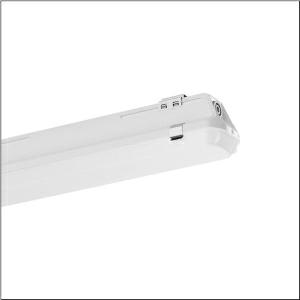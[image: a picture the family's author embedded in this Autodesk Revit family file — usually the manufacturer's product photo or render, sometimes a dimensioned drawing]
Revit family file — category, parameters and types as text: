
# Revit family: monsun_11_51fp12mp480h
name_source: partatom
category: Lighting Fixtures
units: mm (PartAtom-declared; Revit-internal decimal feet)

## family parameters
Cut with Voids When Loaded = No
Host = Face
Light Source = No
Part Type = Normal
Room Calculation Point = No
Round Connector Dimension = Use Diameter
Shared = No

## types (1)
- --- (1 x LED, 7990 lm, 45.4 W, 4000K)
    Apparent Load = 45 VA
    CIE Flux Codes = 65 88 97 97 100
    Color Rendering = 80
    Color Temperature = 4000K
    Default Elevation = 1800 mm
    Description = Monsun 11, damp-proof luminaire, chain hanger, primary light control with lens, primary optical cover: enclosure, of PMMA, light emission: direct distribution, primary light characteristic: symmetric, installation type: suspended mounting, surface-mounted, horizontal mounting, vertical mounting, LED, rated luminous flux: 7.990lm, luminous efficacy: 176lm/W, light colour: 840, colour temperature: 4000K, control gear: ON/OFF Multilumen, with terminal, 3-pole, max. 2.5mm², mains connection: 220..240V, AC, 50/60Hz, rated input power: 45W, luminaire housing, of glass-fibre reinforced polyester, uncoated, bright grey, incl. chain hanger, length: 1.590mm, width: 90mm, height: 88mm, clip for enclosure, of stainless steel (V2A), ceiling mounting element, of stainless steel (V2A), chain hanger, of stainless steel (V2A), protection rating (complete): IP66, insulation class (complete): insulation class I (protective earthing), certification: CE, ENEC, VDE, UKCA, protection symbol: D, impact resistance: IK04, permissible operating ambient temperature: -35..+40°C, standard: EN 50419, EN 60598-2-1, no direct snow, no direct sun, no direct rain, for indoor or canopied outdoor use, corresponds to IFS (International Featured Standards) requirements for safety and quality in the food industry, contact your sales advisor before using the luminaires in applications with unclear chemical exposure, large temperature fluctuations or condensation-forming humidity, LABS conformity tested according to VDMA 24364:2018-05, packaging unit: 1 piece
    Height = 89 mm
    Lamp = 1 x LED
    Lamp Light Flux = 7990 lm
    Lamp Power = 45.4 W
    Lamp count = 1
    Length = 1590 mm
    Luminous efficacy = 176 lm/W
    Manufacturer = Siteco
    ModVariant = No
    Model = 51FP12MP480H
    Mounting Place = Ceiling
    Mounting Type = Surface mounted
    Number of Poles = 1
    OnlyDefault = Yes
    Power Factor = 1
    Product Name = Monsun 11
    Product group = damp-proof luminaire
    ProductGroupID = 300
    Protection Class = Protection class I
    Protection Degree = IP 66
    RLX_Detail_Level = 1
    RLX_Emergency_Light_Flux = 0 lm
    RLX_Emergency_Type = 0
    RLX_Emergency_Type_DB = No
    RlxData = <blob elided: 90221 chars, md5=2f0170d7>
    Socket = socket
    Standby Power = 0 W
    System Light Flux = 7990 lm
    System Power = 45 W
    Type Comments = factory setting: luminous flux: 100 % | (A | C | E) | 105 mA
    Type Image = l_1349237.jpg
    URL = http://relux.com
    VarID = @adj_197483
    Voltage = 0 V
    Weight = 0.00 kg
    Width = 90 mm

## geometry (parser evidence)
native form markers: Blend x4, Sweep x12
no freeform markers — native parametric forms only
